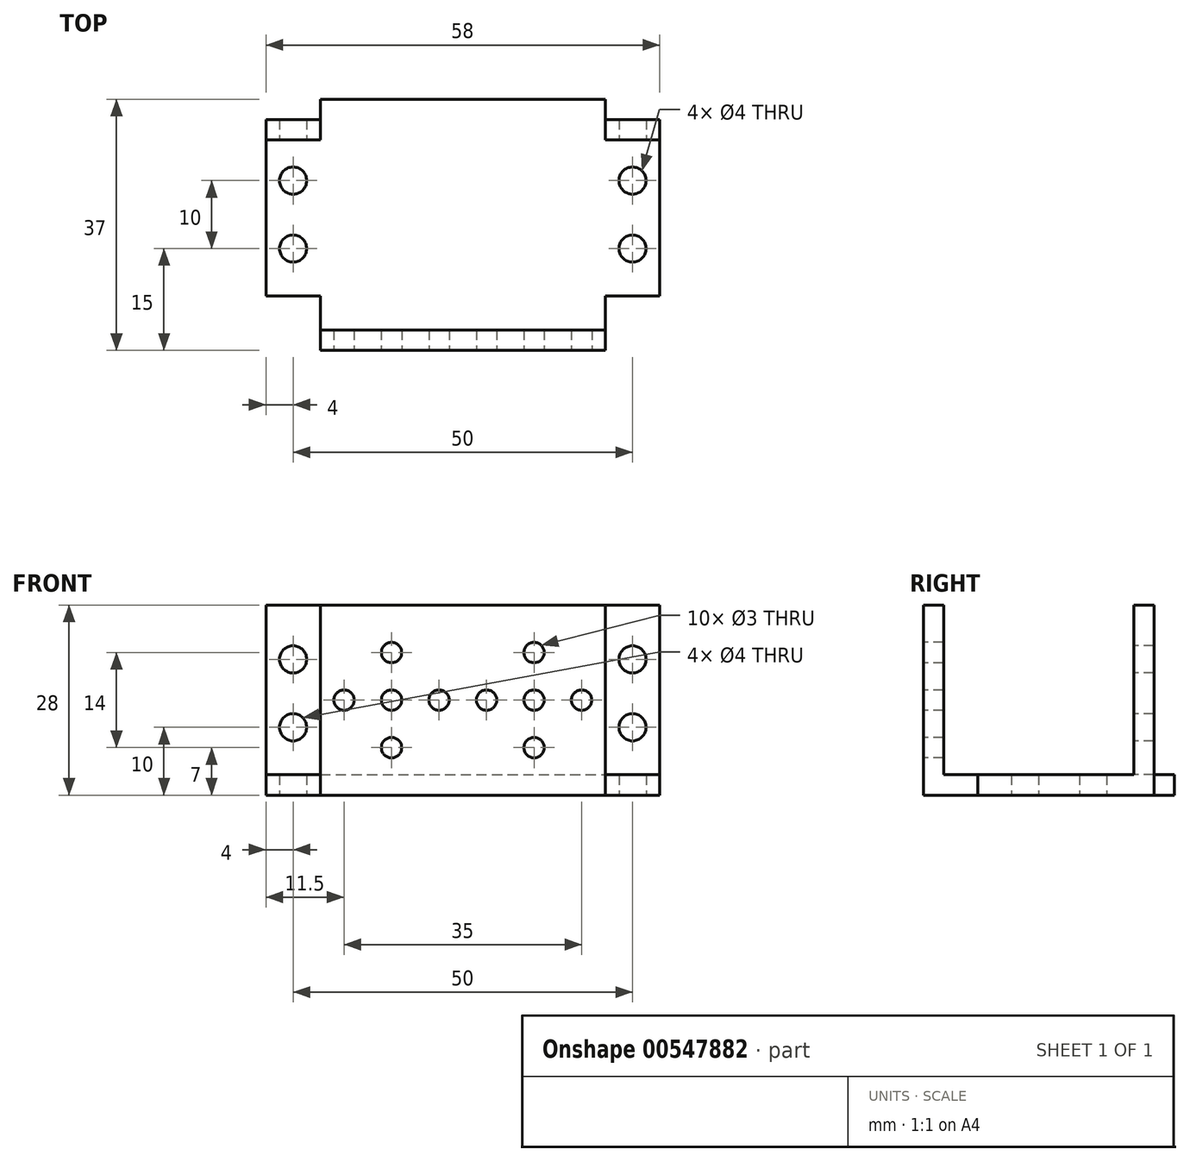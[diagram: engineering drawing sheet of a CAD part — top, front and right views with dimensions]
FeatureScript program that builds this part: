
annotation { "Feature Type Name" : "Feature", "Feature Type Description" : "" }
export const myFeature = defineFeature(function(context is Context, id is Id, definition is map)
    precondition{}
    {
        {
            var Q0;
            Q0=qCreatedBy(makeId("Top.planeOp"),FACE);
            var sketch = newSketch(context, id + "F0", { "sketchPlane" : qUnion([Q0])});
            skLineSegment(sketch, "E0.bottom", {"start": v(0, 0) * mm, "end": v(58, 0) * mm});
            skLineSegment(sketch, "E0.top", {"start": v(0, 37) * mm, "end": v(58, 37) * mm});
            skLineSegment(sketch, "E0.left", {"start": v(0, 0) * mm, "end": v(0, 37) * mm});
            skLineSegment(sketch, "E0.right", {"start": v(58, 0) * mm, "end": v(58, 37) * mm});
            skLineSegment(sketch, "E1", {"start": v(8, 0) * mm, "end": v(8, 8) * mm});
            skLineSegment(sketch, "E2", {"start": v(8, 8) * mm, "end": v(0, 8) * mm});
            skLineSegment(sketch, "E3.bottom", {"start": v(0, 37) * mm, "end": v(8, 37) * mm});
            skLineSegment(sketch, "E3.top", {"start": v(0, 34) * mm, "end": v(8, 34) * mm});
            skLineSegment(sketch, "E3.left", {"start": v(0, 37) * mm, "end": v(0, 34) * mm});
            skLineSegment(sketch, "E3.right", {"start": v(8, 37) * mm, "end": v(8, 34) * mm});
            skLineSegment(sketch, "E4", {"start": v(29, 0) * mm, "end": v(29, 37) * mm, "construction": true});
            skLineSegment(sketch, "E5.MirrorCS", {"start": v(50, 37) * mm, "end": v(50, 34) * mm});
            skLineSegment(sketch, "E6.MirrorCS", {"start": v(58, 34) * mm, "end": v(50, 34) * mm});
            skLineSegment(sketch, "E7.MirrorCS", {"start": v(50, 8) * mm, "end": v(58, 8) * mm});
            skLineSegment(sketch, "E8.MirrorCS", {"start": v(50, 0) * mm, "end": v(50, 8) * mm});
            skSolve(sketch);
        }
        {
            var Q0;
            {var subQ4=sQuery(id+"F0.wireOp",EDGE,"E1");Q0=makeQuery(id+"F0.imprint","IMPRINT",FACE,{"disambiguationData":[TD([[makeQuery(id+"F0.imprint","IMPRINT",EDGE,{"derivedFrom":subQ4}),-1.0]])]});}
            extrude(context, id + "F1", {"entities" : qUnion([Q0]), "depth" : 3 * mm, "offsetDistance" : 25 * mm});
        }
        {
            var Q0;
            Q0=makeQuery(id+"F1.opExtrude","CAP_FACE",FACE,{"disambiguationData":[OSD([sQuery(id+"F0.wireOp",EDGE,"E0.bottom"),sQuery(id+"F0.wireOp",EDGE,"E0.top"),sQuery(id+"F0.wireOp",EDGE,"E0.left"),sQuery(id+"F0.wireOp",EDGE,"E0.right"),sQuery(id+"F0.wireOp",EDGE,"E1"),sQuery(id+"F0.wireOp",EDGE,"E2"),sQuery(id+"F0.wireOp",EDGE,"E3.top"),sQuery(id+"F0.wireOp",EDGE,"E3.right"),sQuery(id+"F0.wireOp",EDGE,"E5.MirrorCS"),sQuery(id+"F0.wireOp",EDGE,"E6.MirrorCS"),sQuery(id+"F0.wireOp",EDGE,"E7.MirrorCS"),sQuery(id+"F0.wireOp",EDGE,"E8.MirrorCS")])],"isStart":false});
            var sketch = newSketch(context, id + "F2", { "sketchPlane" : qUnion([Q0])});
            skLineSegment(sketch, "E9.bottom", {"start": v(8, 0) * mm, "end": v(50, 0) * mm});
            skLineSegment(sketch, "E9.top", {"start": v(8, 3) * mm, "end": v(50, 3) * mm});
            skLineSegment(sketch, "E9.left", {"start": v(8, 0) * mm, "end": v(8, 3) * mm});
            skLineSegment(sketch, "E9.right", {"start": v(50, 0) * mm, "end": v(50, 3) * mm});
            skLineSegment(sketch, "E10.bottom", {"start": v(0, 34) * mm, "end": v(8, 34) * mm});
            skLineSegment(sketch, "E10.top", {"start": v(0, 31) * mm, "end": v(8, 31) * mm});
            skLineSegment(sketch, "E10.left", {"start": v(0, 34) * mm, "end": v(0, 31) * mm});
            skLineSegment(sketch, "E10.right", {"start": v(8, 34) * mm, "end": v(8, 31) * mm});
            skLineSegment(sketch, "E11.bottom", {"start": v(58, 34) * mm, "end": v(50, 34) * mm});
            skLineSegment(sketch, "E11.top", {"start": v(58, 31) * mm, "end": v(50, 31) * mm});
            skLineSegment(sketch, "E11.left", {"start": v(58, 34) * mm, "end": v(58, 31) * mm});
            skLineSegment(sketch, "E11.right", {"start": v(50, 34) * mm, "end": v(50, 31) * mm});
            skSolve(sketch);
        }
        {
            var Q0;
            Q0 = qSketchRegion(id + "F2", true);
            extrude(context, id + "F3", {"entities" : qUnion([Q0]), "operationType" : NewBodyOperationType.ADD, "depth" : 25 * mm, "offsetDistance" : 25 * mm});
        }
        {
            var Q0;
            Q0=qCreatedBy(makeId("Front.planeOp"),FACE);
            var sketch = newSketch(context, id + "F4", { "sketchPlane" : qUnion([Q0])});
            skCircle(sketch, "E12", {"center": v(54, 20) * mm, "radius": 2 * mm});
            skCircle(sketch, "E13", {"center": v(54, 10) * mm, "radius": 2 * mm});
            skCircle(sketch, "E14", {"center": v(4, 20) * mm, "radius": 2 * mm});
            skCircle(sketch, "E15", {"center": v(4, 10) * mm, "radius": 2 * mm});
            skSolve(sketch);
        }
        {
            var Q0;
            Q0 = qSketchRegion(id + "F4", true);
            extrude(context, id + "F5", {"entities" : qUnion([Q0]), "operationType" : NewBodyOperationType.REMOVE, "endBound" : BoundingType.THROUGH_ALL, "oppositeDirection" : true, "depth" : 25 * mm, "offsetDistance" : 25 * mm});
        }
        {
            var Q0;
            Q0=makeQuery(id+"F3.boolean.opBoolean","MERGE",FACE,{"derivedFrom":[makeQuery(id+"F1.opExtrude","SWEPT_FACE",FACE,{"disambiguationData":[OSD([sQuery(id+"F0.wireOp",EDGE,"E0.bottom")])]}),makeQuery(id+"F3.opExtrude","SWEPT_FACE",FACE,{"disambiguationData":[OSD([sQuery(id+"F2.wireOp",EDGE,"E9.bottom")])]})]});
            var sketch = newSketch(context, id + "F6", { "sketchPlane" : qUnion([Q0])});
            skCircle(sketch, "E16", {"center": v(39.5, 14) * mm, "radius": 1.5 * mm});
            skPoint(sketch, "E16.centerSnap0", {"position": v(50, 14) * mm});
            skCircle(sketch, "E17", {"center": v(39.5, 21) * mm, "radius": 1.5 * mm});
            skCircle(sketch, "E18.1.0.0", {"center": v(32.5, 14) * mm, "radius": 1.5 * mm});
            skCircle(sketch, "E18.2.0.0", {"center": v(25.5, 14) * mm, "radius": 1.5 * mm});
            skCircle(sketch, "E18.3.0.0", {"center": v(18.5, 14) * mm, "radius": 1.5 * mm});
            skCircle(sketch, "E18.4.0.0", {"center": v(11.5, 14) * mm, "radius": 1.5 * mm});
            skLineSegment(sketch, "E18.direction1", {"start": v(39.5, 14) * mm, "end": v(32.5, 14) * mm, "construction": true});
            skCircle(sketch, "E19", {"center": v(46.5, 14) * mm, "radius": 1.5 * mm});
            skCircle(sketch, "E20", {"center": v(18.5, 21) * mm, "radius": 1.5 * mm});
            skCircle(sketch, "E21", {"center": v(39.5, 7) * mm, "radius": 1.5 * mm});
            skCircle(sketch, "E22", {"center": v(18.5, 7) * mm, "radius": 1.5 * mm});
            skSolve(sketch);
        }
        {
            var Q0;
            Q0 = qSketchRegion(id + "F6", true);
            extrude(context, id + "F7", {"entities" : qUnion([Q0]), "operationType" : NewBodyOperationType.REMOVE, "endBound" : BoundingType.THROUGH_ALL, "oppositeDirection" : true, "depth" : 25 * mm, "offsetDistance" : 25 * mm});
        }
        {
            var Q0;
            Q0=makeQuery(id+"F1.opExtrude","CAP_FACE",FACE,{"disambiguationData":[OSD([sQuery(id+"F0.wireOp",EDGE,"E0.bottom"),sQuery(id+"F0.wireOp",EDGE,"E0.top"),sQuery(id+"F0.wireOp",EDGE,"E0.left"),sQuery(id+"F0.wireOp",EDGE,"E0.right"),sQuery(id+"F0.wireOp",EDGE,"E1"),sQuery(id+"F0.wireOp",EDGE,"E2"),sQuery(id+"F0.wireOp",EDGE,"E3.top"),sQuery(id+"F0.wireOp",EDGE,"E3.right"),sQuery(id+"F0.wireOp",EDGE,"E5.MirrorCS"),sQuery(id+"F0.wireOp",EDGE,"E6.MirrorCS"),sQuery(id+"F0.wireOp",EDGE,"E7.MirrorCS"),sQuery(id+"F0.wireOp",EDGE,"E8.MirrorCS")])],"isStart":true});
            var sketch = newSketch(context, id + "F8", { "sketchPlane" : qUnion([Q0])});
            skCircle(sketch, "E23", {"center": v(4, -15) * mm, "radius": 2 * mm});
            skCircle(sketch, "E24", {"center": v(4, -25) * mm, "radius": 2 * mm});
            skCircle(sketch, "E25", {"center": v(54, -25) * mm, "radius": 2 * mm});
            skCircle(sketch, "E26", {"center": v(54, -15) * mm, "radius": 2 * mm});
            skSolve(sketch);
        }
        {
            var Q0;
            Q0 = qSketchRegion(id + "F8", true);
            extrude(context, id + "F9", {"entities" : qUnion([Q0]), "operationType" : NewBodyOperationType.REMOVE, "endBound" : BoundingType.THROUGH_ALL, "oppositeDirection" : true, "depth" : 25 * mm, "offsetDistance" : 25 * mm});
        }
    });
